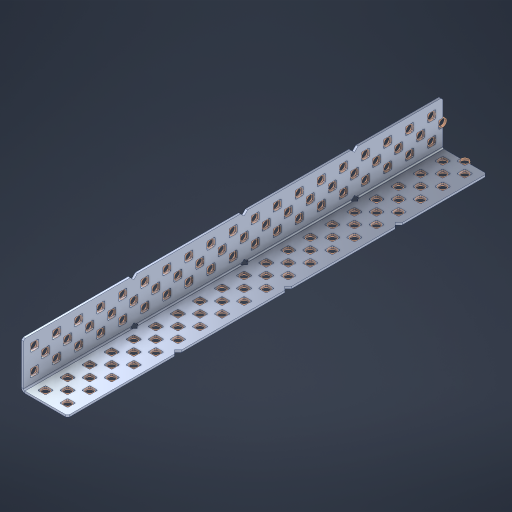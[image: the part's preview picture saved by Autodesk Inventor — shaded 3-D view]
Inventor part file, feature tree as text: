
AUTODESK INVENTOR PART (.ipt)
format: ipt  version: 2023 (Build 270158000, 158)  size: 1,461,248 bytes
history: native  units: in
note: dims shown in document units (in); Inventor stores cm internally (conversion verified against a paired STEP export)
features: other x120, extrude x112, sheet_metal_op x8, sketch x7, pattern_linear x2, mirror x1, chamfer x1
ambient origin geometry x8: Origin, YZ Plane, XZ Plane, XY Plane, X Axis, Y Axis, Z Axis, Center Point
bodies: Solid1 (feature_tree), Body (feature_tree)
feature tree (251):
  sheet_metal_op  "Flanges"
  sheet_metal_op  "Body Pattern"
  pattern_linear  "Center Pattern"  Spacing1=1.0in  [1 undecoded]
  other  "Arc Length"
  pattern_linear  "Notch Pattern"  Spacing1=0.1875in  [1 undecoded]
  other  "Diagonal Plane"
  mirror  "Everything Mirrored"
  chamfer  "End Chamfer"
  sketch  "Sketch1"  dims[d0=1.0in]
  other  "Plate1"
  sketch  "Sketch2"  dims[d1=9.5in]
  other  "Plate2"
  sheet_metal_op  "Bend1"
  sheet_metal_op  "Corner1"
  sketch  "Sketch8"  dims[d2=0.0469in]
  sketch  "Sketch9"  dims[d3=0.0469in]
  other  "Srf91"
  sheet_metal_op  "Body Pattern Sketch"
  other  "Srf92"
  sketch  "Sketch13"  dims[d4=0.0234in]
  sketch  "Sketch15"  dims[d5=0.0938in]
  sketch  "Sketch16"  dims[d6=0.0469in d7=1.0in d8=90.0deg d9=0.0312in d10=0.1875in d11=0.0469in d12=0.0469in d49=0.182in d50=0.02in d52=0.25in d53=0.0469in d54=0.0in d55=0.172in d56=1.0in d57=0.0in d60=7.4803in d62=0.5in d63=0.7874in d65=0.5in d85=0.1473in d86=0.1659in d89=0.0469in d90=0.0in d91=0.04in d92=0.0491in d95=2.5in d96=0.04in d97=0.25in d98=45.0deg d99=0.25in d106=0.182in d107=0.02in d108=0.5in d110=0.0469in d111=0.0in d112=0.172in d113=0.5in d114=0.0in d117=0.5in d123=0.25in d125=0.25in d126=0.0491in d127=0.1227in d128=0.08in d129=0.04in d130=2.5in]
  other  "Srf786"
  other  "Srf856"
  other  "Srf857"
  other  "Srf858"
  other  "Srf859"
  other  "Srf860"
  other  "Srf861"
  other  "Srf889"
  other  "Srf890"
  other  "Srf891"
  other  "Srf1275"
  other  "Srf1276"
  other  "Srf1278"
  other  "Srf1279"
  other  "Srf1280"
  other  "Srf1281"
  other  "Srf1282"
  other  "Srf1283"
  other  "Srf1277"
  other  "Srf1285"
  other  "Srf1286"
  other  "Srf1287"
  other  "Srf1383"
  other  "Srf1384"
  other  "Srf1385"
  other  "Srf1386"
  other  "Srf1387"
  other  "Srf1388"
  other  "Srf1389"
  other  "Srf1390"
  other  "Srf1391"
  other  "Srf1392"
  other  "Srf1393"
  other  "Srf1394"
  other  "Srf1395"
  other  "Srf1396"
  other  "Srf1397"
  other  "Srf1398"
  other  "Srf1399"
  other  "Srf1400"
  other  "Srf1401"
  other  "Srf1402"
  other  "Srf1403"
  other  "Srf1404"
  other  "Srf1405"
  other  "Srf1406"
  other  "Srf1407"
  other  "Srf1408"
  other  "Srf1409"
  other  "Srf1410"
  other  "Srf1411"
  other  "Srf1412"
  other  "Srf1445"
  other  "Srf1446"
  other  "Srf1447"
  other  "Srf1448"
  other  "Srf1449"
  other  "Srf1450"
  other  "Srf1451"
  other  "Srf1452"
  other  "Srf1453"
  other  "Srf1454"
  other  "Srf1455"
  other  "Srf1456"
  other  "Srf1457"
  other  "Srf1458"
  other  "Srf1459"
  other  "Srf1475"
  other  "Srf1476"
  other  "Srf1477"
  other  "Srf1478"
  other  "Srf1479"
  other  "Srf1480"
  other  "Srf1481"
  other  "Srf1482"
  other  "Srf1483"
  other  "Srf1484"
  other  "Srf1485"
  other  "Srf1486"
  other  "Srf1487"
  other  "Srf1488"
  other  "Srf1489"
  other  "Srf1490"
  other  "Srf1491"
  other  "Srf1492"
  other  "Srf1493"
  other  "Srf1494"
  other  "Srf1495"
  other  "Srf1496"
  other  "Srf1497"
  other  "Srf1498"
  other  "Srf1499"
  other  "Srf1500"
  other  "Srf1501"
  other  "Srf1502"
  other  "Srf1503"
  other  "Srf1504"
  other  "Srf1537"
  other  "Srf1538"
  other  "Srf1539"
  other  "Srf1540"
  other  "Srf1541"
  other  "Srf1542"
  other  "Srf1543"
  other  "Srf1544"
  other  "Srf1545"
  other  "Srf1546"
  other  "Srf1547"
  other  "Srf1548"
  other  "Srf1549"
  other  "Srf1550"
  other  "Srf1551"
  sheet_metal_op  "Body Stamp"
  sheet_metal_op  "Body Circle"
  other  "Center Stamp"
  other  "Center Circle"
  sheet_metal_op  "Notch"
  extrude  "ExtrusionSrf92"  Depth=0.0469in
  extrude  "ExtrusionSrf856"  Depth=0.0469in
  extrude  "ExtrusionSrf857"  Depth=0.182in
  extrude  "ExtrusionSrf858"  Depth=0.02in
  extrude  "ExtrusionSrf859"  Depth=0.25in
  extrude  "ExtrusionSrf860"  Depth=0.0469in
  extrude  "ExtrusionSrf861"  TaperAngle=0.0deg  [1 undecoded]
  extrude  "ExtrusionSrf889"  Depth=2.5in
  extrude  "ExtrusionSrf890"  Depth=1.0in TaperAngle=0.0deg
  extrude  "ExtrusionSrf891"  Depth=2.5in
  extrude  "ExtrusionSrf1275"  Depth=0.5in
  extrude  "ExtrusionSrf1276"  Depth=2.5in
  extrude  "ExtrusionSrf1277"  Depth=2.5in
  extrude  "ExtrusionSrf1278"  Depth=0.0469in
  extrude  "ExtrusionSrf1279"  Depth=2.5in TaperAngle=0.0deg
  extrude  "ExtrusionSrf1280"  Depth=2.5in
  extrude  "ExtrusionSrf1281"  Depth=0.25in TaperAngle=45.0deg
  extrude  "ExtrusionSrf1282"  Depth=0.25in
  extrude  "ExtrusionSrf1345"  Depth=0.182in
  extrude  "ExtrusionSrf1346"  Depth=0.02in
  extrude  "ExtrusionSrf1347"  Depth=0.5in
  extrude  "ExtrusionSrf1348"  Depth=0.0469in
  extrude  "ExtrusionSrf1383"  TaperAngle=0.0deg  [1 undecoded]
  extrude  "ExtrusionSrf1384"  Depth=2.5in
  extrude  "ExtrusionSrf1385"  Depth=0.5in TaperAngle=0.0deg
  extrude  "ExtrusionSrf1386"  Depth=0.5in
  extrude  "ExtrusionSrf1387"  Depth=0.25in
  extrude  "ExtrusionSrf1388"  Depth=0.25in
  extrude  "ExtrusionSrf1389"  Depth=2.5in
  extrude  "ExtrusionSrf1390"  Depth=2.5in
  extrude  "ExtrusionSrf1391"  Depth=2.5in
  extrude  "ExtrusionSrf1392"  Depth=2.5in
  extrude  "ExtrusionSrf1393"  Depth=2.5in
  extrude  "ExtrusionSrf1394"  [1 undecoded]
  extrude  "ExtrusionSrf1395"  [1 undecoded]
  extrude  "ExtrusionSrf1396"  [1 undecoded]
  extrude  "ExtrusionSrf1397"  [1 undecoded]
  extrude  "ExtrusionSrf1398"  [1 undecoded]
  extrude  "ExtrusionSrf1399"  [1 undecoded]
  extrude  "ExtrusionSrf1400"  [1 undecoded]
  extrude  "ExtrusionSrf1401"  [1 undecoded]
  extrude  "ExtrusionSrf1402"  [1 undecoded]
  extrude  "ExtrusionSrf1403"  [1 undecoded]
  extrude  "ExtrusionSrf1404"  [1 undecoded]
  extrude  "ExtrusionSrf1405"  [1 undecoded]
  extrude  "ExtrusionSrf1406"  [1 undecoded]
  extrude  "ExtrusionSrf1407"  [1 undecoded]
  extrude  "ExtrusionSrf1408"  [1 undecoded]
  extrude  "ExtrusionSrf1409"  [1 undecoded]
  extrude  "ExtrusionSrf1410"  [1 undecoded]
  extrude  "ExtrusionSrf1411"  [1 undecoded]
  extrude  "ExtrusionSrf1412"  [1 undecoded]
  extrude  "ExtrusionSrf1445"  [1 undecoded]
  extrude  "ExtrusionSrf1446"  [1 undecoded]
  extrude  "ExtrusionSrf1447"  [1 undecoded]
  extrude  "ExtrusionSrf1448"  [1 undecoded]
  extrude  "ExtrusionSrf1449"  [1 undecoded]
  extrude  "ExtrusionSrf1450"  [1 undecoded]
  extrude  "ExtrusionSrf1451"  [1 undecoded]
  extrude  "ExtrusionSrf1452"  [1 undecoded]
  extrude  "ExtrusionSrf1453"  [1 undecoded]
  extrude  "ExtrusionSrf1454"  [1 undecoded]
  extrude  "ExtrusionSrf1455"  [1 undecoded]
  extrude  "ExtrusionSrf1456"  [1 undecoded]
  extrude  "ExtrusionSrf1457"  [1 undecoded]
  extrude  "ExtrusionSrf1458"  [1 undecoded]
  extrude  "ExtrusionSrf1459"  [1 undecoded]
  extrude  "ExtrusionSrf1475"  [1 undecoded]
  extrude  "ExtrusionSrf1476"  [1 undecoded]
  extrude  "ExtrusionSrf1477"  [1 undecoded]
  extrude  "ExtrusionSrf1478"  [1 undecoded]
  extrude  "ExtrusionSrf1479"  [1 undecoded]
  extrude  "ExtrusionSrf1480"  [1 undecoded]
  extrude  "ExtrusionSrf1481"  [1 undecoded]
  extrude  "ExtrusionSrf1482"  [1 undecoded]
  extrude  "ExtrusionSrf1483"  [1 undecoded]
  extrude  "ExtrusionSrf1484"  [1 undecoded]
  extrude  "ExtrusionSrf1485"  [1 undecoded]
  extrude  "ExtrusionSrf1486"  [1 undecoded]
  extrude  "ExtrusionSrf1487"  [1 undecoded]
  extrude  "ExtrusionSrf1488"  [1 undecoded]
  extrude  "ExtrusionSrf1489"  [1 undecoded]
  extrude  "ExtrusionSrf1490"  [1 undecoded]
  extrude  "ExtrusionSrf1491"  [1 undecoded]
  extrude  "ExtrusionSrf1492"  [1 undecoded]
  extrude  "ExtrusionSrf1493"  [1 undecoded]
  extrude  "ExtrusionSrf1494"  [1 undecoded]
  extrude  "ExtrusionSrf1495"  [1 undecoded]
  extrude  "ExtrusionSrf1496"  [1 undecoded]
  extrude  "ExtrusionSrf1497"  [1 undecoded]
  extrude  "ExtrusionSrf1498"  [1 undecoded]
  extrude  "ExtrusionSrf1499"  [1 undecoded]
  extrude  "ExtrusionSrf1500"  [1 undecoded]
  extrude  "ExtrusionSrf1501"  [1 undecoded]
  extrude  "ExtrusionSrf1502"  [1 undecoded]
  extrude  "ExtrusionSrf1503"  [1 undecoded]
  extrude  "ExtrusionSrf1504"  [1 undecoded]
  extrude  "ExtrusionSrf1537"  [1 undecoded]
  extrude  "ExtrusionSrf1538"  [1 undecoded]
  extrude  "ExtrusionSrf1539"  [1 undecoded]
  extrude  "ExtrusionSrf1540"  [1 undecoded]
  extrude  "ExtrusionSrf1541"  [1 undecoded]
  extrude  "ExtrusionSrf1542"  [1 undecoded]
  extrude  "ExtrusionSrf1543"  [1 undecoded]
  extrude  "ExtrusionSrf1544"  [1 undecoded]
  extrude  "ExtrusionSrf1545"  [1 undecoded]
  extrude  "ExtrusionSrf1546"  [1 undecoded]
  extrude  "ExtrusionSrf1547"  [1 undecoded]
  extrude  "ExtrusionSrf1548"  [1 undecoded]
  extrude  "ExtrusionSrf1549"  [1 undecoded]
  extrude  "ExtrusionSrf1550"  [1 undecoded]
  extrude  "ExtrusionSrf1551"  [1 undecoded]
note: 83 required parameter values undecoded (feature->parameter linkage not recoverable at this tier; creation-order binding heuristic only, values carry confidence <= 0.55)
